# Revit family: NLRS_27_GM_LIB_LVI_MR
name_source: partatom
category: Generic Models
units: mm (PartAtom-declared; Revit-internal decimal feet)

## family parameters
Can host rebar = No
Cut with Voids When Loaded = Yes
Part Type = Normal
Room Calculation Point = No
Round Connector Dimension = Use Diameter
Shared = No

## types (4) — shared parameters
01_kraal = Yes
02_Trim = No
03_druppel = Yes
Assembly Code = 27.13
Description = LI Luifel
Hoogte_VK2 = 90 mm  [stored 0.295276 ft]
IfcExportAs = IfcFlowsegment
Manufacturer = Meilof Riks
Model = LI
NLRS_C_Binnenbak = RAL 9010
NLRS_C_Materiaal = RAL 9010
Type Image = <None>
URL = https://www.meilofriks.nl
zero-valued in all types: Default Elevation

## per-type parameters (varying)
| type | Breedte_goot | Diepte_bak | Hoogte_AK | Hoogte_VK | Set_Diepte_bak | set_Hoogte_AK |
| LVI.S365B | 365 mm | 96 mm  [stored 0.314961 ft] | 243 mm | 214 mm | 96 mm  [stored 0.314961 ft] | 243 mm |
| LVI.S500B | 500 mm  [stored 1.64042 ft] | 78 mm  [stored 0.255906 ft] | 236 mm | 207 mm | 78 mm  [stored 0.255906 ft] | 236 mm |
| LVI.S400B | 400 mm  [stored 1.31234 ft] | 78 mm  [stored 0.255906 ft] | 227 mm  [stored 0.744751 ft] | 195 mm  [stored 0.639764 ft] | 78 mm  [stored 0.255906 ft] | 227 mm  [stored 0.744751 ft] |
| LVI.S450B | 450 mm  [stored 1.47638 ft] | 103 mm  [stored 0.337927 ft] | 251 mm  [stored 0.823491 ft] | 221 mm  [stored 0.725066 ft] | 90 mm  [stored 0.295276 ft] | 251 mm  [stored 0.823491 ft] |

note: [stored X ft] marks values corroborated as IEEE doubles in the binary element streams (Revit-internal decimal feet)

## geometry (parser evidence)
native form markers: Sweep x26
no freeform markers — native parametric forms only
